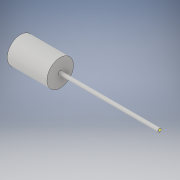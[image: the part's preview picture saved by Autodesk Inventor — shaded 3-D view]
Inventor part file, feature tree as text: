
AUTODESK INVENTOR PART (.ipt)
format: ipt  version: 2018 (Build 220112000, 112)  size: 99,328 bytes
history: native  units: in
note: dims shown in document units (in); Inventor stores cm internally (conversion verified against a paired STEP export)
features: revolve x1, other x1, sketch x1
ambient origin geometry x8: Origin, YZ Plane, XZ Plane, XY Plane, X Axis, Y Axis, Z Axis, Center Point
bodies: Solid1 (feature_tree)
feature tree (3):
  revolve  "Revolution1"  [1 undecoded]
  other  "Work Point1"
  sketch  "Sketch1"  dims[d0=0.125in d1=7.5in d2=1.0in d3=3.0in d4=90.0deg]
note: 1 required parameter value undecoded (feature->parameter linkage not recoverable at this tier; creation-order binding heuristic only, values carry confidence <= 0.55)
